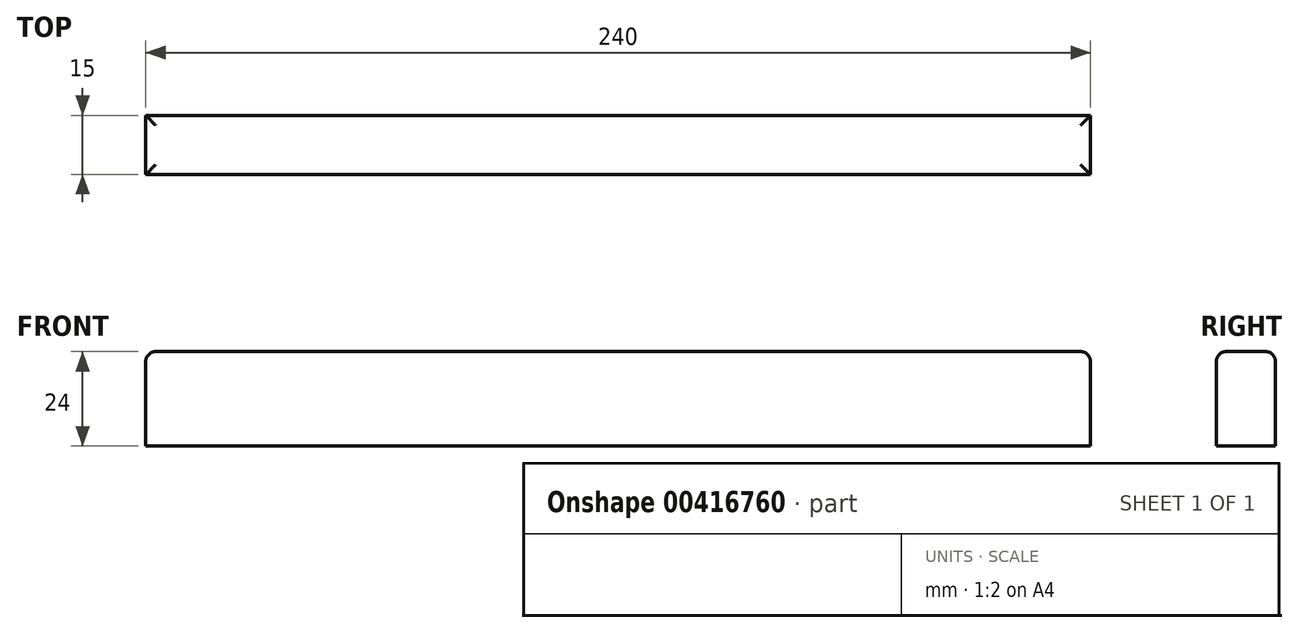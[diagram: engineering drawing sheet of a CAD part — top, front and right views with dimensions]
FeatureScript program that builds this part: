
annotation { "Feature Type Name" : "Feature", "Feature Type Description" : "" }
export const myFeature = defineFeature(function(context is Context, id is Id, definition is map)
    precondition{}
    {
        {
            var Q0;
            Q0=qCreatedBy(makeId("Top.planeOp"),FACE);
            var sketch = newSketch(context, id + "F0", { "sketchPlane" : qUnion([Q0])});
            skLineSegment(sketch, "E0.bottom", {"start": v(0, 0) * mm, "end": v(240, 0) * mm});
            skLineSegment(sketch, "E0.top", {"start": v(0, -15) * mm, "end": v(240, -15) * mm});
            skLineSegment(sketch, "E0.left", {"start": v(0, 0) * mm, "end": v(0, -15) * mm});
            skLineSegment(sketch, "E0.right", {"start": v(240, 0) * mm, "end": v(240, -15) * mm});
            skSolve(sketch);
        }
        {
            var Q0;
            Q0 = qSketchRegion(id + "F0", true);
            extrude(context, id + "F1", {"entities" : qUnion([Q0]), "depth" : 24 * mm});
        }
        {
            var Q0;
            Q0=makeQuery(id+"F1.opExtrude","CAP_EDGE",EDGE,{"disambiguationData":[OSD([sQuery(id+"F0.wireOp",EDGE,"E0.top")])],"isStart":false});
            var Q1;
            Q1=makeQuery(id+"F1.opExtrude","CAP_EDGE",EDGE,{"disambiguationData":[OSD([sQuery(id+"F0.wireOp",EDGE,"E0.bottom")])],"isStart":false});
            var Q2;
            Q2=makeQuery(id+"F1.opExtrude","CAP_EDGE",EDGE,{"disambiguationData":[OSD([sQuery(id+"F0.wireOp",EDGE,"E0.right")])],"isStart":false});
            var Q3;
            Q3=makeQuery(id+"F1.opExtrude","CAP_EDGE",EDGE,{"disambiguationData":[OSD([sQuery(id+"F0.wireOp",EDGE,"E0.left")])],"isStart":false});
            fillet(context, id + "F2", {"entities" : qUnion([Q0, Q1, Q2, Q3]), "radius" : 2.5 * mm, "tangentPropagation" : true, "allowEdgeOverflow" : false});
        }
    });
